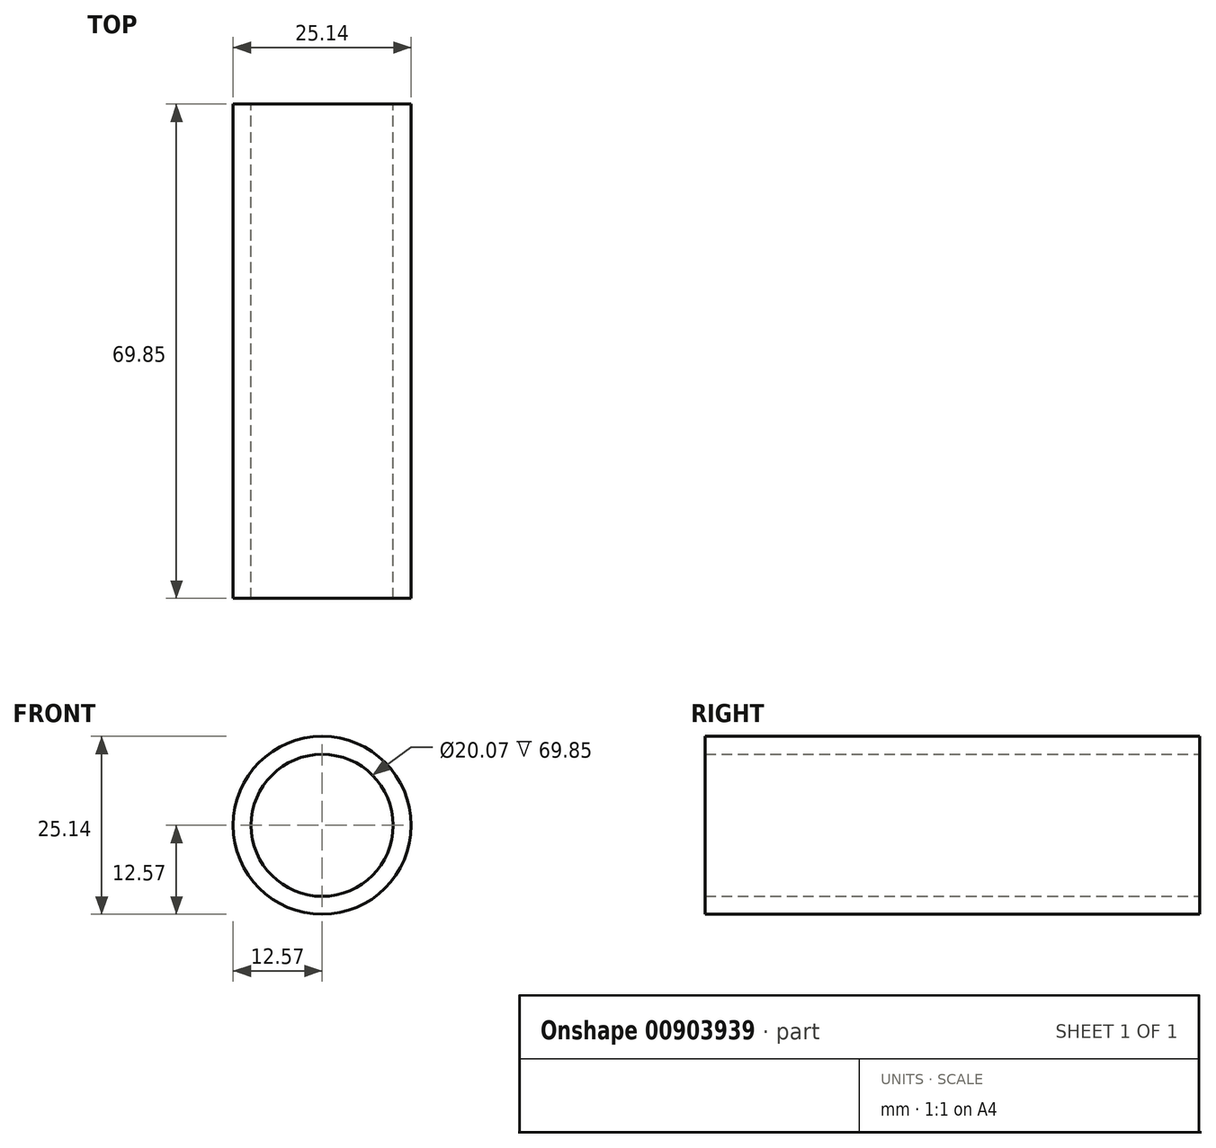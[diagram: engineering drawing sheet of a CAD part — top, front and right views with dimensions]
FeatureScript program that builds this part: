
annotation { "Feature Type Name" : "Feature", "Feature Type Description" : "" }
export const myFeature = defineFeature(function(context is Context, id is Id, definition is map)
    precondition{}
    {
        {
            var Q0;
            Q0=qCreatedBy(makeId("Front.planeOp"),FACE);
            var sketch = newSketch(context, id + "F0", { "sketchPlane" : qUnion([Q0])});
            skCircle(sketch, "E0", {"center": v(0, 0) * mm, "radius": 12.57 * mm});
            skCircle(sketch, "E1", {"center": v(0, 0) * mm, "radius": 10.03 * mm});
            skSolve(sketch);
        }
        {
            var Q0;
            Q0=makeQuery(id+"F0.imprint","IMPRINT",FACE,{"disambiguationData":[TD([[makeQuery(id+"F0.imprint","IMPRINT",EDGE,{"derivedFrom":sQuery(id+"F0.wireOp",EDGE,"E0")}),1.0]])]});
            extrude(context, id + "F1", {"entities" : qUnion([Q0]), "depth" : 69.85 * mm, "offsetDistance" : 25.4 * mm});
        }
    });
